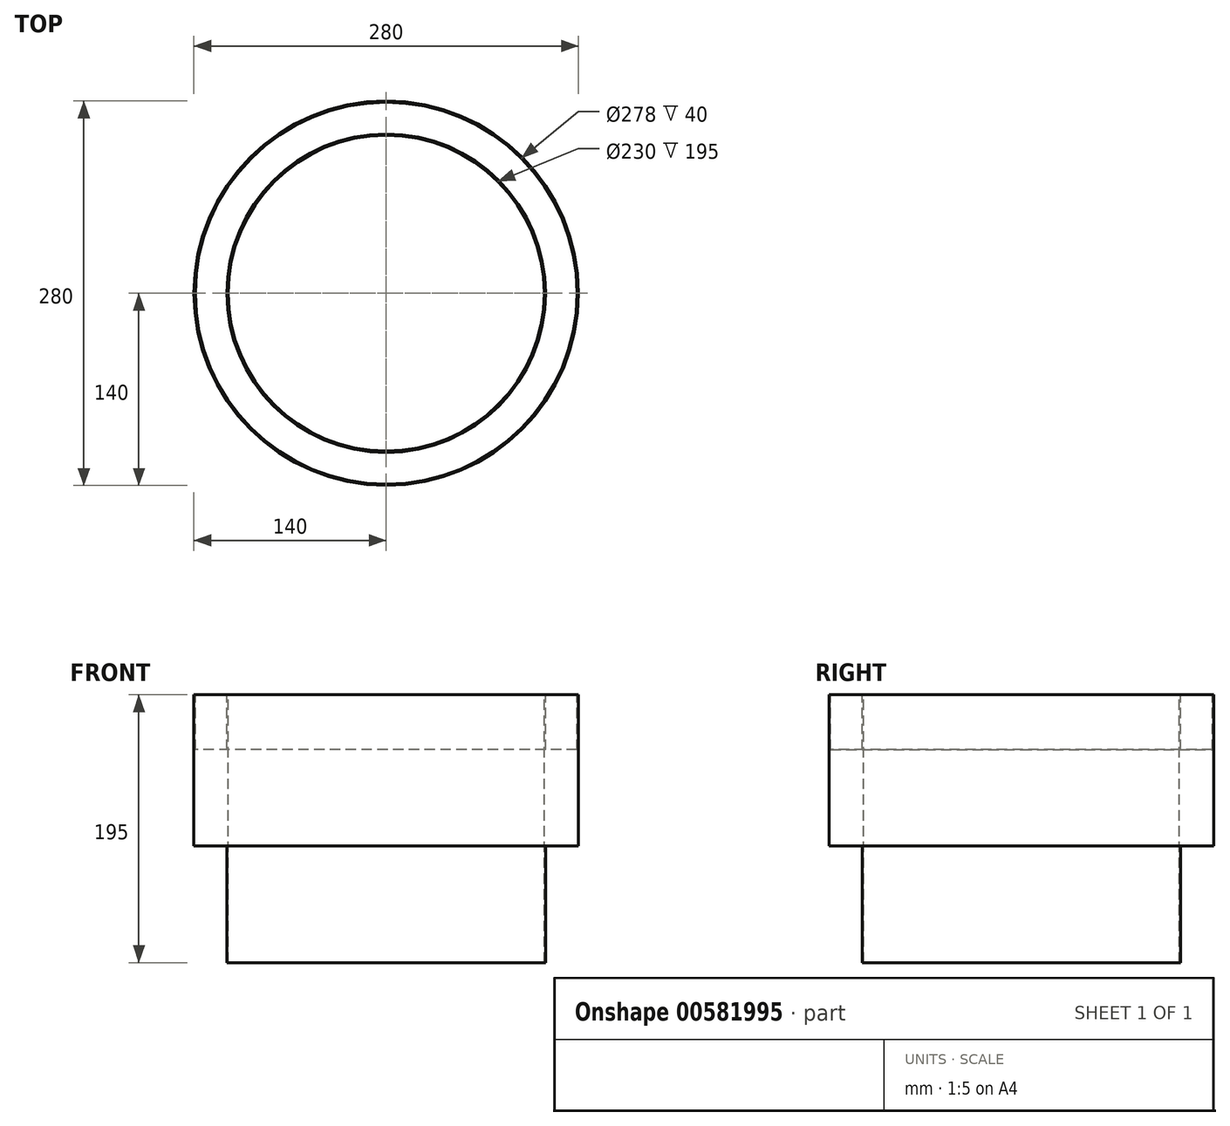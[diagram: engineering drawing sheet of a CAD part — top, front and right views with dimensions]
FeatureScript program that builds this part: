
annotation { "Feature Type Name" : "Feature", "Feature Type Description" : "" }
export const myFeature = defineFeature(function(context is Context, id is Id, definition is map)
    precondition{}
    {
        {
            var Q0;
            Q0=qCreatedBy(makeId("Front.planeOp"),FACE);
            var sketch = newSketch(context, id + "F0", { "sketchPlane" : qUnion([Q0])});
            skLineSegment(sketch, "E0", {"start": v(0, 710.75) * mm, "end": v(0, -704.58) * mm, "construction": true});
            skLineSegment(sketch, "E1", {"start": v(-115, 215.65) * mm, "end": v(-115, 410.65) * mm});
            skLineSegment(sketch, "E2", {"start": v(-115, 410.65) * mm, "end": v(-116, 410.65) * mm});
            skLineSegment(sketch, "E3", {"start": v(-139, 410.65) * mm, "end": v(-140, 410.65) * mm});
            skLineSegment(sketch, "E4", {"start": v(-140, 410.65) * mm, "end": v(-140, 300.65) * mm});
            skLineSegment(sketch, "E5", {"start": v(-140, 300.65) * mm, "end": v(-116, 300.65) * mm});
            skLineSegment(sketch, "E6", {"start": v(-116, 300.65) * mm, "end": v(-116, 215.65) * mm});
            skLineSegment(sketch, "E7", {"start": v(-139, 410.65) * mm, "end": v(-139, 370.65) * mm});
            skLineSegment(sketch, "E8", {"start": v(-139, 370.65) * mm, "end": v(-116, 370.65) * mm});
            skLineSegment(sketch, "E9", {"start": v(-116, 370.65) * mm, "end": v(-116, 410.65) * mm});
            skLineSegment(sketch, "E10", {"start": v(-116, 215.65) * mm, "end": v(-115, 215.65) * mm});
            skSolve(sketch);
        }
        {
            var Q0;
            Q0=qSketchRegion(id+"F0",true);
            var Q1;
            Q1=sQuery(id+"F0.wireOp",EDGE,"E0");
            revolve(context, id + "F1", {"entities" : qUnion([Q0]), "axis" : qUnion([Q1]), "revolveType" : RevolveType.FULL});
        }
    });
